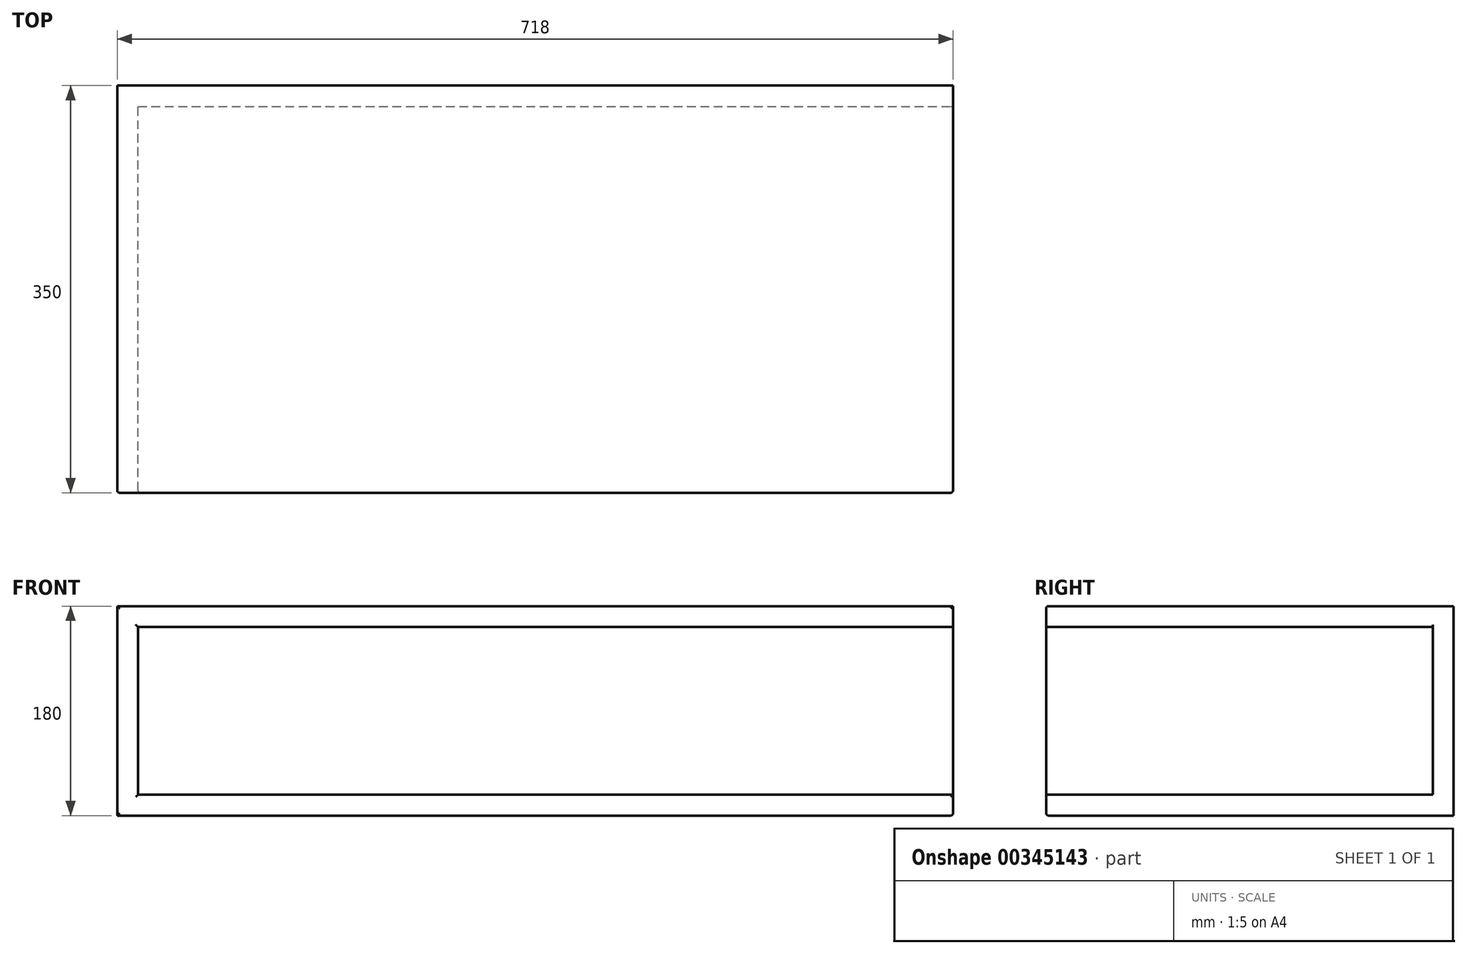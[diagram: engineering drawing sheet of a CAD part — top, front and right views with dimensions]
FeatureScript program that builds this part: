
annotation { "Feature Type Name" : "Feature", "Feature Type Description" : "" }
export const myFeature = defineFeature(function(context is Context, id is Id, definition is map)
    precondition{}
    {
        {
            var Q0;
            Q0=qCreatedBy(makeId("Front.planeOp"),FACE);
            var sketch = newSketch(context, id + "F0", { "sketchPlane" : qUnion([Q0])});
            skLineSegment(sketch, "E0.bottom", {"start": v(0, 0) * mm, "end": v(51.6, 0) * mm});
            skLineSegment(sketch, "E0.top", {"start": v(0, 42.58) * mm, "end": v(51.6, 42.58) * mm});
            skLineSegment(sketch, "E0.left", {"start": v(0, 0) * mm, "end": v(0, 42.58) * mm});
            skLineSegment(sketch, "E0.right", {"start": v(51.6, 0) * mm, "end": v(51.6, 42.58) * mm});
            skSolve(sketch);
        }
        {
            var Q0;
            Q0=makeQuery(id+"F0.imprint","IMPRINT",FACE,{"disambiguationData":[TD([[makeQuery(id+"F0.imprint","IMPRINT",EDGE,{"derivedFrom":sQuery(id+"F0.wireOp",EDGE,"E0.bottom")}),1.0]])]});
            extrude(context, id + "F1", {"entities" : qUnion([Q0]), "depth" : 350 * mm});
        }
        {
            var Q0;
            Q0=makeQuery(id+"F1.opExtrude","SWEPT_FACE",FACE,{"disambiguationData":[OSD([sQuery(id+"F0.wireOp",EDGE,"E0.left")])]});
            extrude(context, id + "F2", {"entities" : qUnion([Q0]), "operationType" : NewBodyOperationType.ADD, "oppositeDirection" : true, "depth" : 718 * mm});
        }
        {
            var Q0;
            {var subQ0=sQuery(id+"F0.wireOp",EDGE,"E0.bottom");Q0=makeQuery(id+"F2.boolean.opBoolean","MERGE",FACE,{"derivedFrom":[makeQuery(id+"F1.opExtrude","SWEPT_FACE",FACE,{"disambiguationData":[OSD([subQ0])]}),makeQuery(id+"F2.opExtrude","SWEPT_FACE",FACE,{"disambiguationData":[OSD([subQ0,sQuery(id+"F0.wireOp",EDGE,"E0.left")])]})]});}
            extrude(context, id + "F3", {"entities" : qUnion([Q0]), "operationType" : NewBodyOperationType.ADD, "oppositeDirection" : true, "depth" : 180 * mm});
        }
        {
            var Q0;
            {var subQ0=sQuery(id+"F0.wireOp",EDGE,"E0.left");var subQ1=sQuery(id+"F0.wireOp",EDGE,"E0.bottom");Q0=makeQuery(id+"F3.boolean.opBoolean","MERGE",FACE,{"derivedFrom":[makeQuery(id+"F2.boolean.opBoolean","MERGE",FACE,{"derivedFrom":[makeQuery(id+"F1.opExtrude","CAP_FACE",FACE,{"disambiguationData":[OSD([subQ1,sQuery(id+"F0.wireOp",EDGE,"E0.top"),subQ0,sQuery(id+"F0.wireOp",EDGE,"E0.right")])],"isStart":false}),makeQuery(id+"F2.opExtrude","SWEPT_FACE",FACE,{"disambiguationData":[OSD([subQ0]),TDD([makeQuery(id+"F1.opExtrude","CAP_EDGE",EDGE,{"disambiguationData":[OSD([subQ0])],"isStart":false})])]})]}),makeQuery(id+"F3.opExtrude","SWEPT_FACE",FACE,{"disambiguationData":[OSD([subQ1,subQ0]),TDD([makeQuery(id+"F2.boolean.opBoolean","MERGE",EDGE,{"derivedFrom":[makeQuery(id+"F1.opExtrude","CAP_EDGE",EDGE,{"disambiguationData":[OSD([subQ1])],"isStart":false}),makeQuery(id+"F2.opExtrude","SWEPT_EDGE",EDGE,{"disambiguationData":[OSD([subQ1,subQ0]),TDD([makeQuery(id+"F1.opExtrude","CAP_VERTEX",VERTEX,{"disambiguationData":[OSD([subQ1,subQ0])],"isStart":false})])]})]})])]})]});}
            var Q1;
            {var subQ0=sQuery(id+"F0.wireOp",EDGE,"E0.left");var subQ1=sQuery(id+"F0.wireOp",EDGE,"E0.bottom");Q1=makeQuery(id+"F3.boolean.opBoolean","MERGE",FACE,{"derivedFrom":[makeQuery(id+"F2.opExtrude","CAP_FACE",FACE,{"disambiguationData":[OSD([subQ0])],"isStart":false}),makeQuery(id+"F3.opExtrude","SWEPT_FACE",FACE,{"disambiguationData":[OSD([subQ1,subQ0]),TDD([makeQuery(id+"F2.opExtrude","CAP_EDGE",EDGE,{"disambiguationData":[OSD([subQ1,subQ0])],"isStart":false})])]})]});}
            shell(context, id + "F4", {"entities" : qUnion([Q0, Q1]), "thickness" : 18 * mm});
        }
        {
            var Q0;
            {var subQ0=sQuery(id+"F0.wireOp",EDGE,"E0.left");var subQ1=sQuery(id+"F0.wireOp",EDGE,"E0.bottom");Q0=makeQuery(id+"F3.opExtrude","CAP_EDGE",EDGE,{"disambiguationData":[OSD([subQ1,subQ0]),TDD([makeQuery(id+"F2.boolean.opBoolean","MERGE",EDGE,{"derivedFrom":[makeQuery(id+"F1.opExtrude","CAP_EDGE",EDGE,{"disambiguationData":[OSD([subQ1])],"isStart":false}),makeQuery(id+"F2.opExtrude","SWEPT_EDGE",EDGE,{"disambiguationData":[OSD([subQ1,subQ0]),TDD([makeQuery(id+"F1.opExtrude","CAP_VERTEX",VERTEX,{"disambiguationData":[OSD([subQ1,subQ0])],"isStart":false})])]})]})])],"isStart":false});}
            var Q1;
            {var subQ0=sQuery(id+"F0.wireOp",EDGE,"E0.left");var subQ1=sQuery(id+"F0.wireOp",EDGE,"E0.bottom");Q1=makeQuery(id+"F3.boolean.opBoolean","MERGE",EDGE,{"derivedFrom":[makeQuery(id+"F1.opExtrude","CAP_EDGE",EDGE,{"disambiguationData":[OSD([subQ0])],"isStart":false}),makeQuery(id+"F3.opExtrude","SWEPT_EDGE",EDGE,{"disambiguationData":[OSD([subQ1,subQ0]),TDD([makeQuery(id+"F1.opExtrude","CAP_VERTEX",VERTEX,{"disambiguationData":[OSD([subQ1,subQ0])],"isStart":false})])]})]});}
            var Q2;
            {var subQ0=sQuery(id+"F0.wireOp",EDGE,"E0.left");var subQ1=sQuery(id+"F0.wireOp",EDGE,"E0.bottom");Q2=makeQuery(id+"F2.boolean.opBoolean","MERGE",EDGE,{"derivedFrom":[makeQuery(id+"F1.opExtrude","CAP_EDGE",EDGE,{"disambiguationData":[OSD([subQ1])],"isStart":false}),makeQuery(id+"F2.opExtrude","SWEPT_EDGE",EDGE,{"disambiguationData":[OSD([subQ1,subQ0]),TDD([makeQuery(id+"F1.opExtrude","CAP_VERTEX",VERTEX,{"disambiguationData":[OSD([subQ1,subQ0])],"isStart":false})])]})]});}
            var Q3;
            {var subQ0=sQuery(id+"F0.wireOp",EDGE,"E0.left");var subQ1=sQuery(id+"F0.wireOp",EDGE,"E0.bottom");Q3=makeQuery(id+"F4.opShell","OFFSET_EDGE",EDGE,{"disambiguationData":[OSD([subQ1,subQ0]),TDD([makeQuery(id+"F3.boolean.opBoolean","MERGE",EDGE,{"derivedFrom":[makeQuery(id+"F2.opExtrude","CAP_EDGE",EDGE,{"disambiguationData":[OSD([subQ0]),TDD([makeQuery(id+"F1.opExtrude","CAP_EDGE",EDGE,{"disambiguationData":[OSD([subQ0])],"isStart":false})])],"isStart":false}),makeQuery(id+"F3.opExtrude","SWEPT_EDGE",EDGE,{"disambiguationData":[OSD([subQ1,subQ0]),TDD([makeQuery(id+"F2.opExtrude","CAP_VERTEX",VERTEX,{"disambiguationData":[OSD([subQ1,subQ0]),TDD([makeQuery(id+"F1.opExtrude","CAP_VERTEX",VERTEX,{"disambiguationData":[OSD([subQ1,subQ0])],"isStart":false})])],"isStart":false})])]})]})])]});}
            fillet(context, id + "F5", {"entities" : qUnion([Q0, Q1, Q2, Q3]), "radius" : 2 * mm, "tangentPropagation" : true, "allowEdgeOverflow" : false});
        }
        {
            var Q0;
            {var subQ0=sQuery(id+"F0.wireOp",EDGE,"E0.left");var subQ1=sQuery(id+"F0.wireOp",EDGE,"E0.bottom");Q0=makeQuery(id+"F4.opShell","OFFSET_EDGE",EDGE,{"disambiguationData":[OSD([subQ1,subQ0]),TDD([makeQuery(id+"F2.boolean.opBoolean","MERGE",EDGE,{"derivedFrom":[makeQuery(id+"F1.opExtrude","CAP_EDGE",EDGE,{"disambiguationData":[OSD([subQ1])],"isStart":false}),makeQuery(id+"F2.opExtrude","SWEPT_EDGE",EDGE,{"disambiguationData":[OSD([subQ1,subQ0]),TDD([makeQuery(id+"F1.opExtrude","CAP_VERTEX",VERTEX,{"disambiguationData":[OSD([subQ1,subQ0])],"isStart":false})])]})]})])]});}
            var Q1;
            {var subQ0=sQuery(id+"F0.wireOp",EDGE,"E0.left");var subQ1=sQuery(id+"F0.wireOp",EDGE,"E0.bottom");Q1=makeQuery(id+"F4.opShell","OFFSET_EDGE",EDGE,{"disambiguationData":[OSD([subQ1,subQ0]),TDD([makeQuery(id+"F3.opExtrude","CAP_EDGE",EDGE,{"disambiguationData":[OSD([subQ1,subQ0]),TDD([makeQuery(id+"F2.boolean.opBoolean","MERGE",EDGE,{"derivedFrom":[makeQuery(id+"F1.opExtrude","CAP_EDGE",EDGE,{"disambiguationData":[OSD([subQ1])],"isStart":false}),makeQuery(id+"F2.opExtrude","SWEPT_EDGE",EDGE,{"disambiguationData":[OSD([subQ1,subQ0]),TDD([makeQuery(id+"F1.opExtrude","CAP_VERTEX",VERTEX,{"disambiguationData":[OSD([subQ1,subQ0])],"isStart":false})])]})]})])],"isStart":false})])]});}
            var Q2;
            {var subQ0=sQuery(id+"F0.wireOp",EDGE,"E0.left");var subQ1=sQuery(id+"F0.wireOp",EDGE,"E0.bottom");Q2=makeQuery(id+"F4.opShell","OFFSET_EDGE",EDGE,{"disambiguationData":[OSD([subQ1,subQ0]),TDD([makeQuery(id+"F3.boolean.opBoolean","MERGE",EDGE,{"derivedFrom":[makeQuery(id+"F1.opExtrude","CAP_EDGE",EDGE,{"disambiguationData":[OSD([subQ0])],"isStart":false}),makeQuery(id+"F3.opExtrude","SWEPT_EDGE",EDGE,{"disambiguationData":[OSD([subQ1,subQ0]),TDD([makeQuery(id+"F1.opExtrude","CAP_VERTEX",VERTEX,{"disambiguationData":[OSD([subQ1,subQ0])],"isStart":false})])]})]})])]});}
            var Q3;
            {var subQ0=sQuery(id+"F0.wireOp",EDGE,"E0.left");var subQ1=sQuery(id+"F0.wireOp",EDGE,"E0.bottom");Q3=makeQuery(id+"F3.boolean.opBoolean","MERGE",EDGE,{"derivedFrom":[makeQuery(id+"F2.opExtrude","CAP_EDGE",EDGE,{"disambiguationData":[OSD([subQ0]),TDD([makeQuery(id+"F1.opExtrude","CAP_EDGE",EDGE,{"disambiguationData":[OSD([subQ0])],"isStart":false})])],"isStart":false}),makeQuery(id+"F3.opExtrude","SWEPT_EDGE",EDGE,{"disambiguationData":[OSD([subQ1,subQ0]),TDD([makeQuery(id+"F2.opExtrude","CAP_VERTEX",VERTEX,{"disambiguationData":[OSD([subQ1,subQ0]),TDD([makeQuery(id+"F1.opExtrude","CAP_VERTEX",VERTEX,{"disambiguationData":[OSD([subQ1,subQ0])],"isStart":false})])],"isStart":false})])]})]});}
            fillet(context, id + "F6", {"entities" : qUnion([Q0, Q1, Q2, Q3]), "radius" : 2 * mm, "tangentPropagation" : true, "allowEdgeOverflow" : false});
        }
    });
